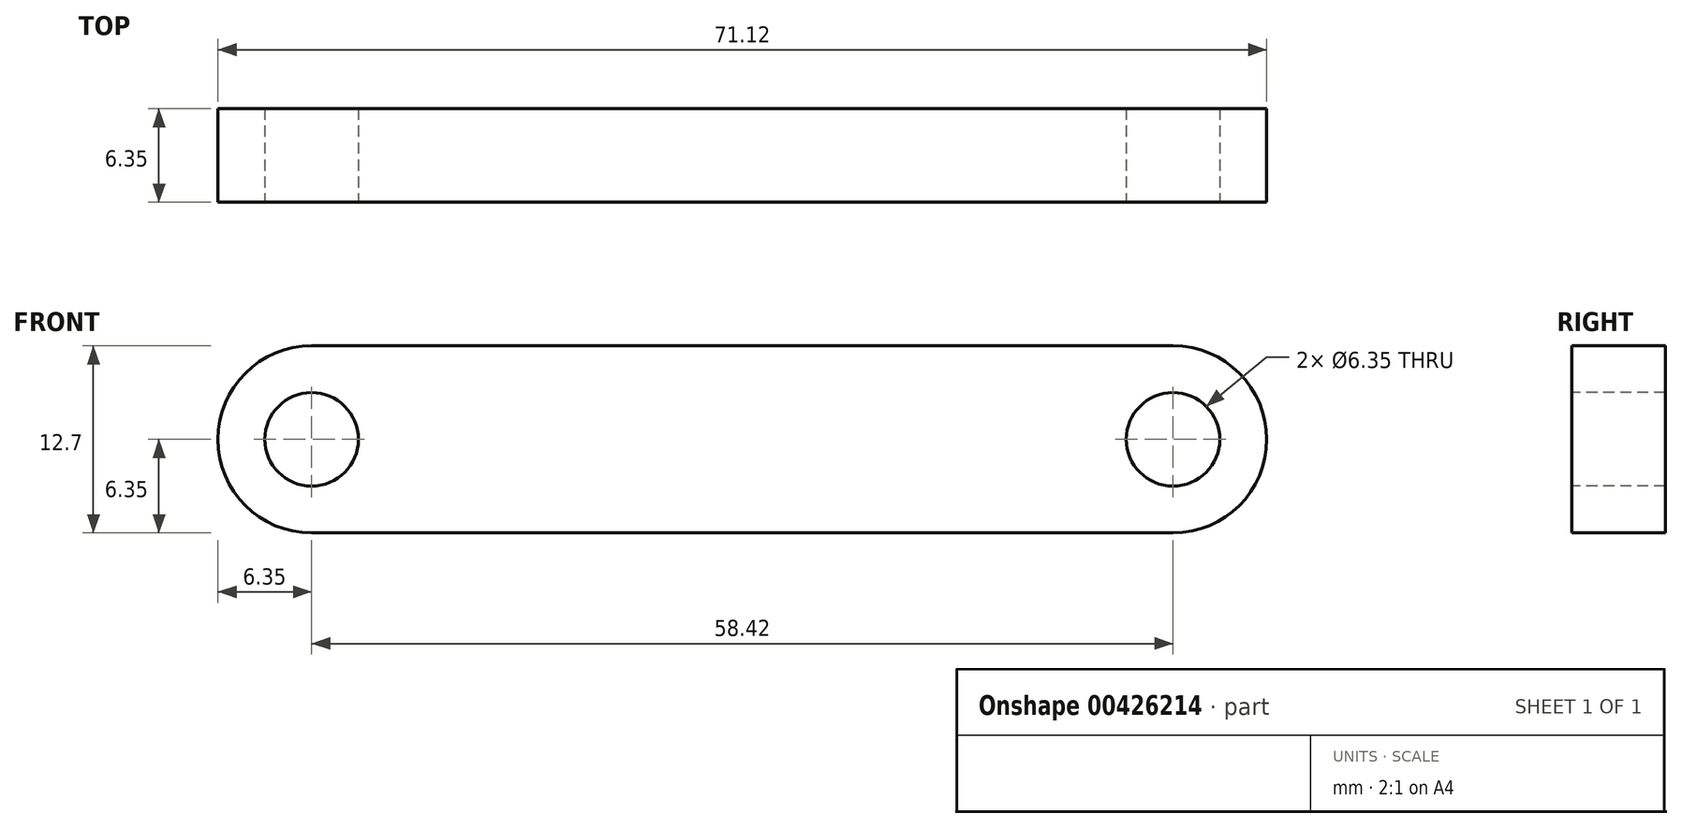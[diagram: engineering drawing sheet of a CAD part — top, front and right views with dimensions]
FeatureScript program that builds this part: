
annotation { "Feature Type Name" : "Feature", "Feature Type Description" : "" }
export const myFeature = defineFeature(function(context is Context, id is Id, definition is map)
    precondition{}
    {
        {
            var Q0;
            Q0=qCreatedBy(makeId("Front.planeOp"),FACE);
            var sketch = newSketch(context, id + "F0", { "sketchPlane" : qUnion([Q0])});
            skLineSegment(sketch, "E0.bottom", {"start": v(0, 0) * mm, "end": v(71.12, 0) * mm});
            skLineSegment(sketch, "E0.top", {"start": v(0, 12.7) * mm, "end": v(71.12, 12.7) * mm});
            skLineSegment(sketch, "E0.left", {"start": v(0, 0) * mm, "end": v(0, 12.7) * mm});
            skLineSegment(sketch, "E0.right", {"start": v(71.12, 0) * mm, "end": v(71.12, 12.7) * mm});
            skSolve(sketch);
        }
        {
            var Q0;
            Q0 = qSketchRegion(id + "F0", true);
            extrude(context, id + "F1", {"entities" : qUnion([Q0]), "depth" : 6.35 * mm});
        }
        {
            var Q0;
            Q0=makeQuery(id+"F1.opExtrude","SWEPT_EDGE",EDGE,{"disambiguationData":[OSD([sQuery(id+"F0.wireOp",EDGE,"E0.top"),sQuery(id+"F0.wireOp",EDGE,"E0.right")])]});
            var Q1;
            Q1=makeQuery(id+"F1.opExtrude","SWEPT_EDGE",EDGE,{"disambiguationData":[OSD([sQuery(id+"F0.wireOp",EDGE,"E0.bottom"),sQuery(id+"F0.wireOp",EDGE,"E0.right")])]});
            var Q2;
            Q2=makeQuery(id+"F1.opExtrude","SWEPT_EDGE",EDGE,{"disambiguationData":[OSD([sQuery(id+"F0.wireOp",EDGE,"E0.top"),sQuery(id+"F0.wireOp",EDGE,"E0.left")])]});
            var Q3;
            Q3=makeQuery(id+"F1.opExtrude","SWEPT_EDGE",EDGE,{"disambiguationData":[OSD([sQuery(id+"F0.wireOp",EDGE,"E0.bottom"),sQuery(id+"F0.wireOp",EDGE,"E0.left")])]});
            fillet(context, id + "F2", {"entities" : qUnion([Q0, Q1, Q2, Q3]), "radius" : 6.35 * mm, "tangentPropagation" : true, "allowEdgeOverflow" : false});
        }
        {
            var Q0;
            Q0=makeQuery(id+"F1.opExtrude","CAP_FACE",FACE,{"disambiguationData":[OSD([sQuery(id+"F0.wireOp",EDGE,"E0.bottom"),sQuery(id+"F0.wireOp",EDGE,"E0.top"),sQuery(id+"F0.wireOp",EDGE,"E0.left"),sQuery(id+"F0.wireOp",EDGE,"E0.right")])],"isStart":false});
            var sketch = newSketch(context, id + "F3", { "sketchPlane" : qUnion([Q0])});
            skCircle(sketch, "E1", {"center": v(6.35, 6.35) * mm, "radius": 3.18 * mm});
            skCircle(sketch, "E2", {"center": v(64.77, 6.35) * mm, "radius": 3.18 * mm});
            skSolve(sketch);
        }
        {
            var Q0;
            Q0 = qSketchRegion(id + "F3", true);
            extrude(context, id + "F4", {"entities" : qUnion([Q0]), "operationType" : NewBodyOperationType.REMOVE, "endBound" : BoundingType.THROUGH_ALL, "oppositeDirection" : true, "depth" : 25.4 * mm});
        }
    });
